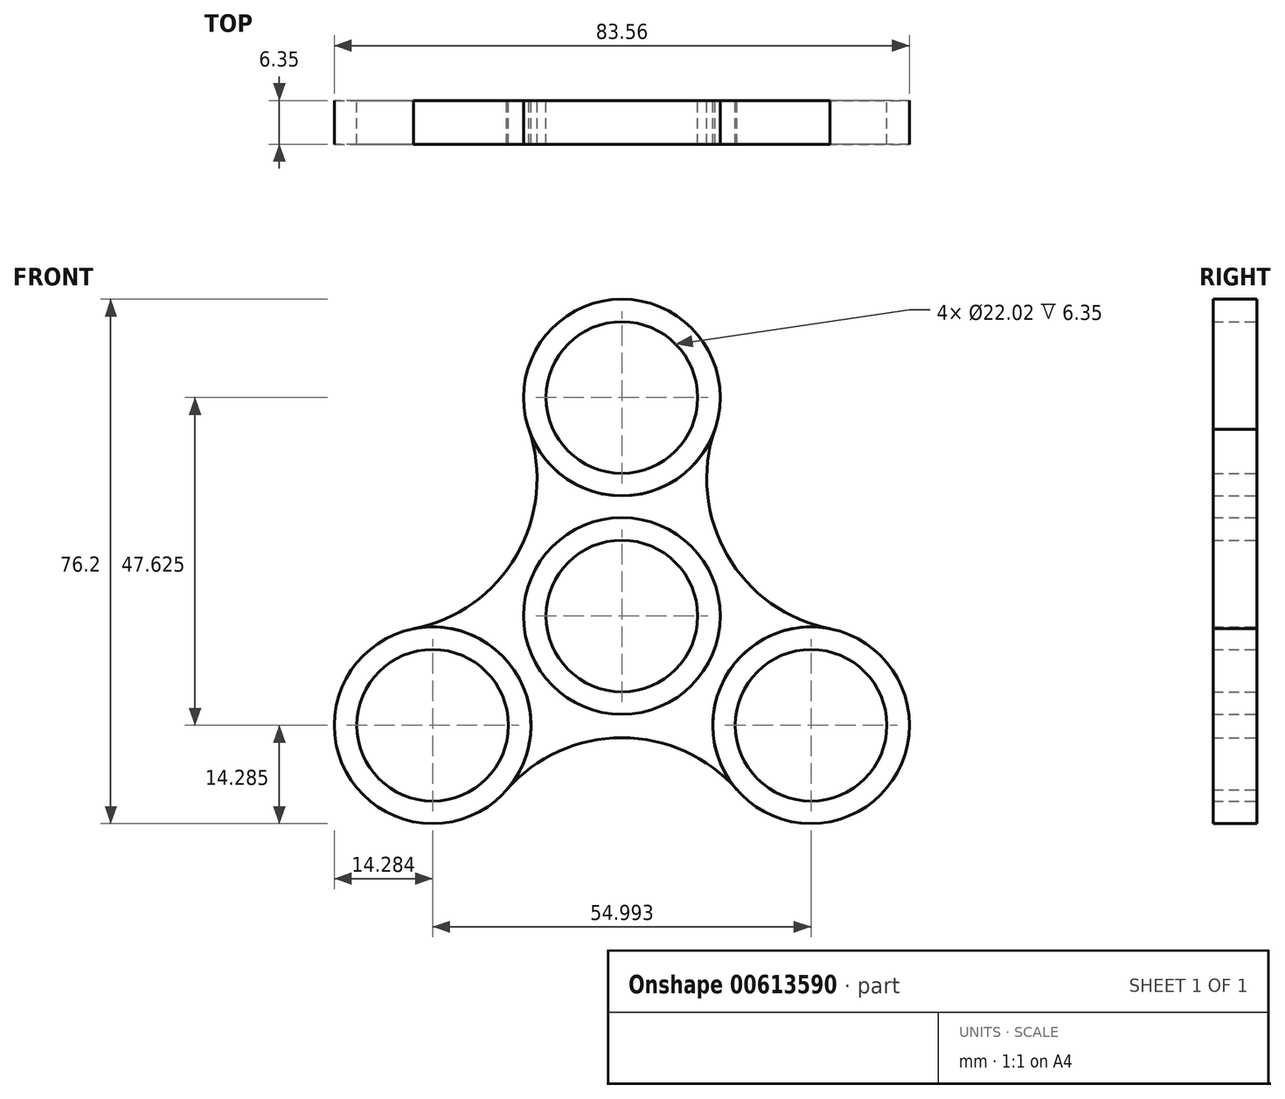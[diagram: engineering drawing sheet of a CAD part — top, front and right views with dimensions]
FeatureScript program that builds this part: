
annotation { "Feature Type Name" : "Feature", "Feature Type Description" : "" }
export const myFeature = defineFeature(function(context is Context, id is Id, definition is map)
    precondition{}
    {
        {
            var Q0;
            Q0=qCreatedBy(makeId("Front.planeOp"),FACE);
            var sketch = newSketch(context, id + "F0", { "sketchPlane" : qUnion([Q0])});
            skCircle(sketch, "E0", {"center": v(0, 0) * mm, "radius": 14.29 * mm});
            skCircle(sketch, "E1", {"center": v(0, 31.75) * mm, "radius": 14.29 * mm});
            skCircle(sketch, "E2", {"center": v(0, 31.75) * mm, "radius": 11.01 * mm});
            skCircle(sketch, "E3", {"center": v(0, 0) * mm, "radius": 11.01 * mm});
            skCircle(sketch, "E4.1.0", {"center": v(-27.5, -15.87) * mm, "radius": 14.29 * mm});
            skCircle(sketch, "E4.1.1", {"center": v(-27.5, -15.87) * mm, "radius": 11.01 * mm});
            skCircle(sketch, "E4.2.0", {"center": v(27.5, -15.88) * mm, "radius": 14.29 * mm});
            skCircle(sketch, "E4.2.1", {"center": v(27.5, -15.88) * mm, "radius": 11.01 * mm});
            skSolve(sketch);
        }
        {
            var Q0;
            Q0=qCreatedBy(makeId("Front.planeOp"),FACE);
            var sketch = newSketch(context, id + "F1", { "sketchPlane" : qUnion([Q0])});
            skArc(sketch, "E5", {"start": v(-30.26, -1.86) * mm, "mid": v(-15.3, 8.84) * mm, "end": v(-13.52, 27.13) * mm});
            skArc(sketch, "E6", {"start": v(13.52, 27.13) * mm, "mid": v(15.3, 8.84) * mm, "end": v(30.26, -1.86) * mm});
            skArc(sketch, "E7", {"start": v(16.74, -25.28) * mm, "mid": v(0, -17.67) * mm, "end": v(-16.74, -25.28) * mm});
            skCircle(sketch, "E8", {"center": v(-27.5, -15.87) * mm, "radius": 14.29 * mm});
            skCircle(sketch, "E9", {"center": v(-27.5, -15.87) * mm, "radius": 11.01 * mm});
            skCircle(sketch, "E10", {"center": v(0, 31.75) * mm, "radius": 14.29 * mm});
            skCircle(sketch, "E11", {"center": v(0, 31.75) * mm, "radius": 11.01 * mm});
            skCircle(sketch, "E12", {"center": v(27.5, -15.88) * mm, "radius": 14.29 * mm});
            skCircle(sketch, "E13", {"center": v(27.5, -15.88) * mm, "radius": 11.01 * mm});
            skSolve(sketch);
        }
        {
            var Q0;
            {var subQ1=sQuery(id+"F1.wireOp",EDGE,"E5");Q0=makeQuery(id+"F1.imprint","IMPRINT",FACE,{"disambiguationData":[TD([[makeQuery(id+"F1.imprint","IMPRINT",EDGE,{"derivedFrom":subQ1}),-1.0]])]});}
            var Q1;
            Q1=makeQuery(id+"F0.imprint","IMPRINT",FACE,{"disambiguationData":[TD([[makeQuery(id+"F0.imprint","IMPRINT",EDGE,{"derivedFrom":sQuery(id+"F0.wireOp",EDGE,"E4.2.0")}),1.0]])]});
            var Q2;
            Q2=makeQuery(id+"F0.imprint","IMPRINT",FACE,{"disambiguationData":[TD([[makeQuery(id+"F0.imprint","IMPRINT",EDGE,{"derivedFrom":sQuery(id+"F0.wireOp",EDGE,"E0")}),1.0]])]});
            var Q3;
            Q3=makeQuery(id+"F0.imprint","IMPRINT",FACE,{"disambiguationData":[TD([[makeQuery(id+"F0.imprint","IMPRINT",EDGE,{"derivedFrom":sQuery(id+"F0.wireOp",EDGE,"E4.1.0")}),1.0]])]});
            var Q4;
            Q4=makeQuery(id+"F0.imprint","IMPRINT",FACE,{"disambiguationData":[TD([[makeQuery(id+"F0.imprint","IMPRINT",EDGE,{"derivedFrom":sQuery(id+"F0.wireOp",EDGE,"E1")}),1.0]])]});
            extrude(context, id + "F2", {"entities" : qUnion([Q0, Q1, Q2, Q3, Q4]), "depth" : 6.35 * mm, "offsetDistance" : 25.4 * mm});
        }
    });
